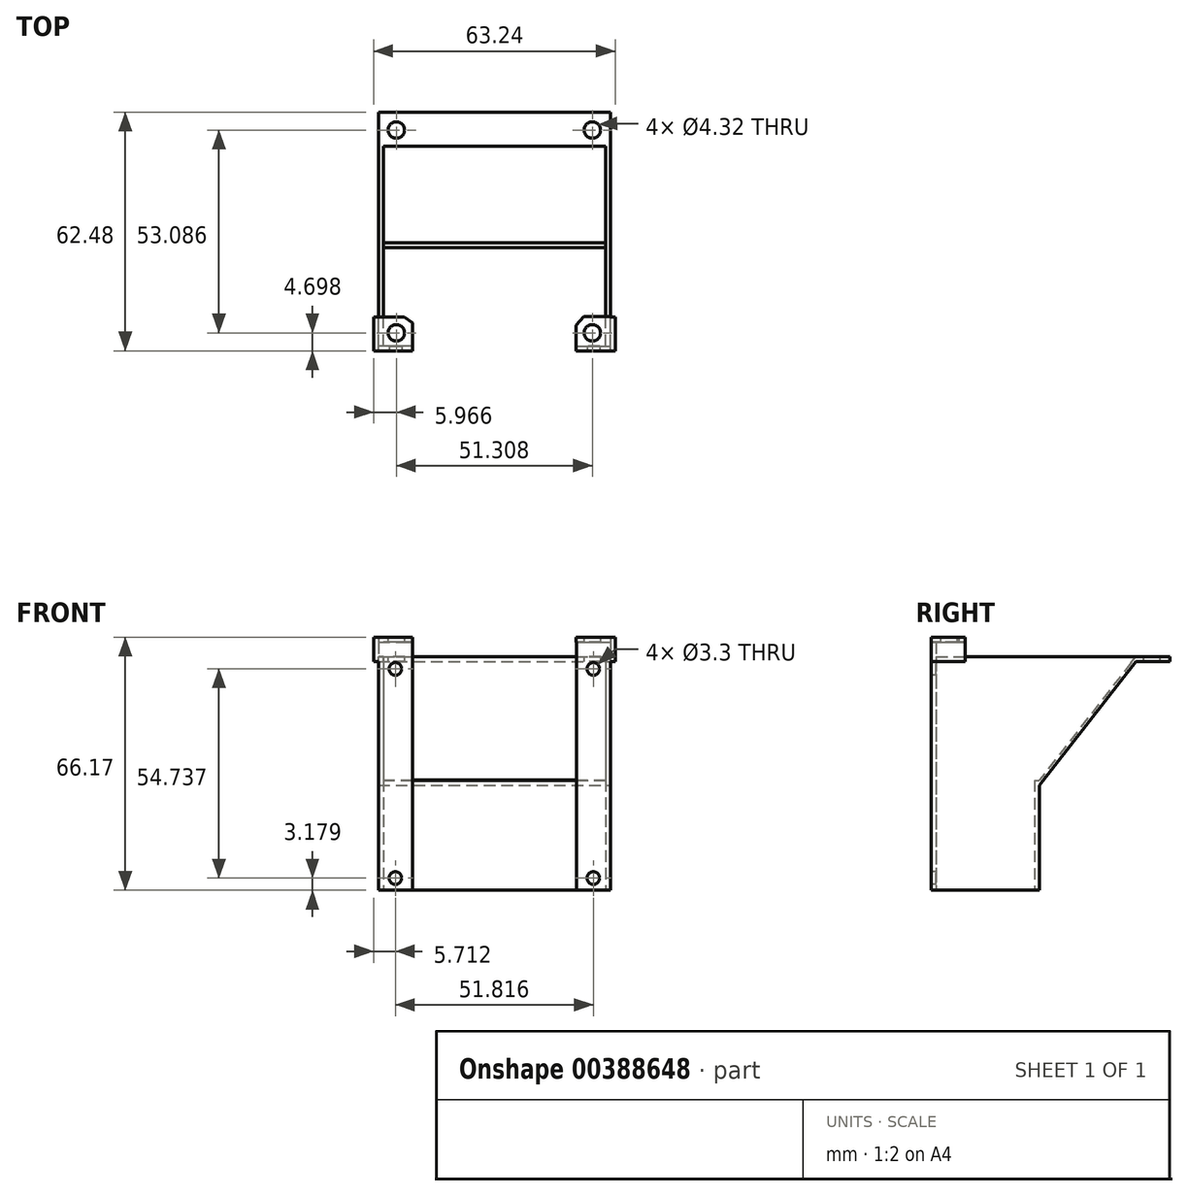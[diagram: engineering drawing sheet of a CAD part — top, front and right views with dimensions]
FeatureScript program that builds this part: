
annotation { "Feature Type Name" : "Feature", "Feature Type Description" : "" }
export const myFeature = defineFeature(function(context is Context, id is Id, definition is map)
    precondition{}
    {
        {
            var Q0;
            Q0=qCreatedBy(makeId("Front.planeOp"),FACE);
            var sketch = newSketch(context, id + "F0", { "sketchPlane" : qUnion([Q0])});
            skLineSegment(sketch, "E0.bottom", {"start": v(-29.08, 14.38) * mm, "end": v(29.08, 14.38) * mm});
            skLineSegment(sketch, "E0.top", {"start": v(-29.08, -14.38) * mm, "end": v(29.08, -14.38) * mm});
            skLineSegment(sketch, "E0.left", {"start": v(-29.08, 14.38) * mm, "end": v(-29.08, -14.38) * mm});
            skLineSegment(sketch, "E0.right", {"start": v(29.08, 14.38) * mm, "end": v(29.08, -14.38) * mm});
            skPoint(sketch, "E0.middle", {"position": v(0, 0) * mm});
            skLineSegment(sketch, "E1.bottom", {"start": v(29.08, -14.38) * mm, "end": v(30.35, -14.38) * mm});
            skLineSegment(sketch, "E1.top", {"start": v(29.08, 46.71) * mm, "end": v(30.35, 46.71) * mm});
            skLineSegment(sketch, "E1.left", {"start": v(29.08, -14.38) * mm, "end": v(29.08, 46.71) * mm});
            skLineSegment(sketch, "E1.right", {"start": v(30.35, -14.38) * mm, "end": v(30.35, 46.71) * mm});
            skLineSegment(sketch, "E2.bottom", {"start": v(-29.08, -14.38) * mm, "end": v(-30.35, -14.38) * mm});
            skLineSegment(sketch, "E2.top", {"start": v(-29.08, 46.71) * mm, "end": v(-30.35, 46.71) * mm});
            skLineSegment(sketch, "E2.left", {"start": v(-29.08, -14.38) * mm, "end": v(-29.08, 46.71) * mm});
            skLineSegment(sketch, "E2.right", {"start": v(-30.35, -14.38) * mm, "end": v(-30.35, 46.71) * mm});
            skSolve(sketch);
        }
        {
            var Q0;
            {var subQ0=sQuery(id+"F0.wireOp",EDGE,"E0.bottom");Q0=makeQuery(id+"F0.imprint","IMPRINT",FACE,{"disambiguationData":[TD([[makeQuery(id+"F0.imprint","IMPRINT",EDGE,{"derivedFrom":subQ0}),-1.0]])]});}
            extrude(context, id + "F1", {"entities" : qUnion([Q0]), "depth" : 1.27 * mm});
        }
        {
            var Q0;
            {var subQ3=sQuery(id+"F0.wireOp",EDGE,"E1.bottom");Q0=makeQuery(id+"F0.imprint","IMPRINT",FACE,{"disambiguationData":[TD([[makeQuery(id+"F0.imprint","IMPRINT",EDGE,{"derivedFrom":subQ3}),1.0]])]});}
            var Q1;
            {var subQ3=sQuery(id+"F0.wireOp",EDGE,"E2.bottom");Q1=makeQuery(id+"F0.imprint","IMPRINT",FACE,{"disambiguationData":[TD([[makeQuery(id+"F0.imprint","IMPRINT",EDGE,{"derivedFrom":subQ3}),-1.0]])]});}
            extrude(context, id + "F2", {"entities" : qUnion([Q0, Q1]), "operationType" : NewBodyOperationType.ADD, "depth" : 28.32 * mm});
        }
        {
            var Q0;
            Q0=makeQuery(id+"F2.opExtrude","SWEPT_FACE",FACE,{"disambiguationData":[OSD([sQuery(id+"F0.wireOp",EDGE,"E1.right")])]});
            var sketch = newSketch(context, id + "F3", { "sketchPlane" : qUnion([Q0])});
            skLineSegment(sketch, "E3.bottom", {"start": v(0, 46.71) * mm, "end": v(34.16, 46.71) * mm});
            skLineSegment(sketch, "E3.right", {"start": v(34.16, 46.71) * mm, "end": v(34.16, 45.44) * mm});
            skLineSegment(sketch, "E4", {"start": v(0, 13.1) * mm, "end": v(25.27, 45.44) * mm});
            skLineSegment(sketch, "E5", {"start": v(24.04, 45.16) * mm, "end": v(0, 14.4) * mm});
            skLineSegment(sketch, "E6", {"start": v(24.04, 45.16) * mm, "end": v(25.27, 46.71) * mm});
            skLineSegment(sketch, "E7", {"start": v(25.27, 45.44) * mm, "end": v(34.16, 45.44) * mm});
            skLineSegment(sketch, "E8", {"start": v(0, 46.71) * mm, "end": v(0, 14.4) * mm});
            skSolve(sketch);
        }
        {
            var Q0;
            {var subQ0=sQuery(id+"F3.wireOp",EDGE,"E4");Q0=makeQuery(id+"F3.imprint","IMPRINT",FACE,{"disambiguationData":[TD([[makeQuery(id+"F3.imprint","IMPRINT",EDGE,{"derivedFrom":subQ0}),1.0]])]});}
            extrude(context, id + "F4", {"entities" : qUnion([Q0]), "operationType" : NewBodyOperationType.ADD, "oppositeDirection" : true, "depth" : 60.7 * mm});
        }
        {
            var Q0;
            Q0=makeQuery(id+"F3.imprint","IMPRINT",FACE,{"disambiguationData":[TD([[makeQuery(id+"F3.imprint","IMPRINT",EDGE,{"derivedFrom":sQuery(id+"F3.wireOp",EDGE,"E5")}),-1.0]])]});
            extrude(context, id + "F5", {"entities" : qUnion([Q0]), "operationType" : NewBodyOperationType.ADD, "oppositeDirection" : true, "depth" : 1.27 * mm});
        }
        {
            var Q0;
            Q0=makeQuery(id+"F4.boolean.opBoolean","MERGE",FACE,{"derivedFrom":[makeQuery(id+"F2.opExtrude","SWEPT_FACE",FACE,{"disambiguationData":[OSD([sQuery(id+"F0.wireOp",EDGE,"E2.right")])]}),makeQuery(id+"F4.opExtrude","CAP_FACE",FACE,{"disambiguationData":[OSD([sQuery(id+"F0.wireOp",EDGE,"E1.right"),sQuery(id+"F3.wireOp",EDGE,"E3.bottom"),sQuery(id+"F3.wireOp",EDGE,"E3.right"),sQuery(id+"F3.wireOp",EDGE,"E4"),sQuery(id+"F3.wireOp",EDGE,"E5"),sQuery(id+"F3.wireOp",EDGE,"E6"),sQuery(id+"F3.wireOp",EDGE,"E7")])],"isStart":false})]});
            var sketch = newSketch(context, id + "F6", { "sketchPlane" : qUnion([Q0])});
            skLineSegment(sketch, "E9", {"start": v(-25.27, 46.71) * mm, "end": v(0, 46.71) * mm});
            skLineSegment(sketch, "E10", {"start": v(0, 46.71) * mm, "end": v(0, 14.4) * mm});
            skLineSegment(sketch, "E11", {"start": v(0, 14.4) * mm, "end": v(-25.27, 46.71) * mm});
            skSolve(sketch);
        }
        {
            var Q0;
            Q0=qSketchRegion(id+"F6",true);
            extrude(context, id + "F7", {"entities" : qUnion([Q0]), "operationType" : NewBodyOperationType.ADD, "oppositeDirection" : true, "depth" : 1.27 * mm});
        }
        {
            var Q0;
            {var subQ0=sQuery(id+"F3.wireOp",EDGE,"E3.bottom");Q0=makeQuery(id+"F7.boolean.opBoolean","MERGE",FACE,{"derivedFrom":[makeQuery(id+"F2.opExtrude","SWEPT_FACE",FACE,{"disambiguationData":[OSD([sQuery(id+"F0.wireOp",EDGE,"E2.top")])]}),makeQuery(id+"F5.boolean.opBoolean","MERGE",FACE,{"derivedFrom":[makeQuery(id+"F2.opExtrude","SWEPT_FACE",FACE,{"disambiguationData":[OSD([sQuery(id+"F0.wireOp",EDGE,"E1.top")])]}),makeQuery(id+"F4.opExtrude","SWEPT_FACE",FACE,{"disambiguationData":[OSD([subQ0])]}),makeQuery(id+"F5.opExtrude","SWEPT_FACE",FACE,{"disambiguationData":[OSD([subQ0])]})]}),makeQuery(id+"F7.opExtrude","SWEPT_FACE",FACE,{"disambiguationData":[OSD([sQuery(id+"F6.wireOp",EDGE,"E9")])]})]});}
            var sketch = newSketch(context, id + "F8", { "sketchPlane" : qUnion([Q0])});
            skCircle(sketch, "E12", {"center": v(-25.65, 29.46) * mm, "radius": 2.16 * mm});
            skCircle(sketch, "E13", {"center": v(25.65, 29.46) * mm, "radius": 2.16 * mm});
            skSolve(sketch);
        }
        {
            var Q0;
            Q0=qSketchRegion(id+"F8",true);
            extrude(context, id + "F9", {"entities" : qUnion([Q0]), "operationType" : NewBodyOperationType.REMOVE, "oppositeDirection" : true, "depth" : 1.27 * mm});
        }
        {
            var Q0;
            Q0=makeQuery(id+"F5.boolean.opBoolean","MERGE",FACE,{"derivedFrom":[makeQuery(id+"F2.opExtrude","SWEPT_FACE",FACE,{"disambiguationData":[OSD([sQuery(id+"F0.wireOp",EDGE,"E1.left")])]}),makeQuery(id+"F5.opExtrude","CAP_FACE",FACE,{"disambiguationData":[OSD([sQuery(id+"F3.wireOp",EDGE,"E3.bottom"),sQuery(id+"F3.wireOp",EDGE,"E5"),sQuery(id+"F3.wireOp",EDGE,"E6"),sQuery(id+"F3.wireOp",EDGE,"E8")])],"isStart":false})]});
            var sketch = newSketch(context, id + "F10", { "sketchPlane" : qUnion([Q0])});
            skLineSegment(sketch, "E14.bottom", {"start": v(28.32, 46.71) * mm, "end": v(27.05, 46.71) * mm});
            skLineSegment(sketch, "E14.top", {"start": v(28.32, -14.38) * mm, "end": v(27.05, -14.38) * mm});
            skLineSegment(sketch, "E14.left", {"start": v(28.32, 46.71) * mm, "end": v(28.32, -14.38) * mm});
            skLineSegment(sketch, "E14.right", {"start": v(27.05, 46.71) * mm, "end": v(27.05, -14.38) * mm});
            skSolve(sketch);
        }
        {
            var Q0;
            Q0=qSketchRegion(id+"F10",true);
            extrude(context, id + "F11", {"entities" : qUnion([Q0]), "operationType" : NewBodyOperationType.ADD, "depth" : 7.62 * mm});
        }
        {
            var Q0;
            Q0=makeQuery(id+"F7.boolean.opBoolean","MERGE",FACE,{"derivedFrom":[makeQuery(id+"F2.opExtrude","SWEPT_FACE",FACE,{"disambiguationData":[OSD([sQuery(id+"F0.wireOp",EDGE,"E2.left")])]}),makeQuery(id+"F7.opExtrude","CAP_FACE",FACE,{"disambiguationData":[OSD([sQuery(id+"F6.wireOp",EDGE,"E9"),sQuery(id+"F6.wireOp",EDGE,"E10"),sQuery(id+"F6.wireOp",EDGE,"E11")])],"isStart":false})]});
            var sketch = newSketch(context, id + "F12", { "sketchPlane" : qUnion([Q0])});
            skLineSegment(sketch, "E15.bottom", {"start": v(-28.32, 46.71) * mm, "end": v(-27.05, 46.71) * mm});
            skLineSegment(sketch, "E15.top", {"start": v(-28.32, -14.38) * mm, "end": v(-27.05, -14.38) * mm});
            skLineSegment(sketch, "E15.left", {"start": v(-28.32, 46.71) * mm, "end": v(-28.32, -14.38) * mm});
            skLineSegment(sketch, "E15.right", {"start": v(-27.05, 46.71) * mm, "end": v(-27.05, -14.38) * mm});
            skSolve(sketch);
        }
        {
            var Q0;
            Q0=qSketchRegion(id+"F12",true);
            extrude(context, id + "F13", {"entities" : qUnion([Q0]), "operationType" : NewBodyOperationType.ADD, "depth" : 7.62 * mm});
        }
        {
            var Q0;
            Q0=makeQuery(id+"F13.boolean.opBoolean","MERGE",FACE,{"derivedFrom":[makeQuery(id+"F2.opExtrude","CAP_FACE",FACE,{"disambiguationData":[OSD([sQuery(id+"F0.wireOp",EDGE,"E2.bottom"),sQuery(id+"F0.wireOp",EDGE,"E2.top"),sQuery(id+"F0.wireOp",EDGE,"E2.left"),sQuery(id+"F0.wireOp",EDGE,"E2.right")])],"isStart":false}),makeQuery(id+"F13.opExtrude","SWEPT_FACE",FACE,{"disambiguationData":[OSD([sQuery(id+"F12.wireOp",EDGE,"E15.left")])]})]});
            var sketch = newSketch(context, id + "F14", { "sketchPlane" : qUnion([Q0])});
            skCircle(sketch, "E16", {"center": v(-25.9, 43.54) * mm, "radius": 1.65 * mm});
            skCircle(sketch, "E17", {"center": v(25.9, 43.54) * mm, "radius": 1.65 * mm});
            skCircle(sketch, "E18", {"center": v(-25.9, -11.2) * mm, "radius": 1.65 * mm});
            skCircle(sketch, "E19", {"center": v(25.9, -11.2) * mm, "radius": 1.65 * mm});
            skSolve(sketch);
        }
        {
            var Q0;
            Q0=makeQuery(id+"F14.imprint","IMPRINT",FACE,{"disambiguationData":[TD([[makeQuery(id+"F14.imprint","IMPRINT",EDGE,{"derivedFrom":sQuery(id+"F14.wireOp",EDGE,"E19")}),1.0]])]});
            var Q1;
            Q1=makeQuery(id+"F14.imprint","IMPRINT",FACE,{"disambiguationData":[TD([[makeQuery(id+"F14.imprint","IMPRINT",EDGE,{"derivedFrom":sQuery(id+"F14.wireOp",EDGE,"E18")}),1.0]])]});
            var Q2;
            Q2=makeQuery(id+"F14.imprint","IMPRINT",FACE,{"disambiguationData":[TD([[makeQuery(id+"F14.imprint","IMPRINT",EDGE,{"derivedFrom":sQuery(id+"F14.wireOp",EDGE,"E16")}),1.0]])]});
            var Q3;
            Q3=makeQuery(id+"F14.imprint","IMPRINT",FACE,{"disambiguationData":[TD([[makeQuery(id+"F14.imprint","IMPRINT",EDGE,{"derivedFrom":sQuery(id+"F14.wireOp",EDGE,"E17")}),1.0]])]});
            extrude(context, id + "F15", {"entities" : qUnion([Q0, Q1, Q2, Q3]), "operationType" : NewBodyOperationType.REMOVE, "oppositeDirection" : true, "depth" : 1.27 * mm});
        }
        {
            var Q0;
            {var subQ0=sQuery(id+"F3.wireOp",EDGE,"E3.bottom");Q0=makeQuery(id+"F13.boolean.opBoolean","MERGE",FACE,{"derivedFrom":[makeQuery(id+"F11.boolean.opBoolean","MERGE",FACE,{"derivedFrom":[makeQuery(id+"F7.boolean.opBoolean","MERGE",FACE,{"derivedFrom":[makeQuery(id+"F2.opExtrude","SWEPT_FACE",FACE,{"disambiguationData":[OSD([sQuery(id+"F0.wireOp",EDGE,"E2.top")])]}),makeQuery(id+"F5.boolean.opBoolean","MERGE",FACE,{"derivedFrom":[makeQuery(id+"F2.opExtrude","SWEPT_FACE",FACE,{"disambiguationData":[OSD([sQuery(id+"F0.wireOp",EDGE,"E1.top")])]}),makeQuery(id+"F4.opExtrude","SWEPT_FACE",FACE,{"disambiguationData":[OSD([subQ0])]}),makeQuery(id+"F5.opExtrude","SWEPT_FACE",FACE,{"disambiguationData":[OSD([subQ0])]})]}),makeQuery(id+"F7.opExtrude","SWEPT_FACE",FACE,{"disambiguationData":[OSD([sQuery(id+"F6.wireOp",EDGE,"E9")])]})]}),makeQuery(id+"F11.opExtrude","SWEPT_FACE",FACE,{"disambiguationData":[OSD([sQuery(id+"F10.wireOp",EDGE,"E14.bottom")])]})]}),makeQuery(id+"F13.opExtrude","SWEPT_FACE",FACE,{"disambiguationData":[OSD([sQuery(id+"F12.wireOp",EDGE,"E15.bottom")])]})]});}
            var sketch = newSketch(context, id + "F16", { "sketchPlane" : qUnion([Q0])});
            skLineSegment(sketch, "E20.bottom", {"start": v(-21.46, -28.32) * mm, "end": v(-30.35, -28.32) * mm});
            skLineSegment(sketch, "E20.top", {"start": v(-21.46, -27.05) * mm, "end": v(-30.35, -27.05) * mm});
            skLineSegment(sketch, "E20.left", {"start": v(-21.46, -28.32) * mm, "end": v(-21.46, -27.05) * mm});
            skLineSegment(sketch, "E20.right", {"start": v(-30.35, -28.32) * mm, "end": v(-30.35, -27.05) * mm});
            skLineSegment(sketch, "E21.bottom", {"start": v(21.46, -28.32) * mm, "end": v(30.35, -28.32) * mm});
            skLineSegment(sketch, "E21.top", {"start": v(21.46, -27.05) * mm, "end": v(30.35, -27.05) * mm});
            skLineSegment(sketch, "E21.left", {"start": v(21.46, -28.32) * mm, "end": v(21.46, -27.05) * mm});
            skLineSegment(sketch, "E21.right", {"start": v(30.35, -28.32) * mm, "end": v(30.35, -27.05) * mm});
            skSolve(sketch);
        }
        {
            var Q0;
            Q0=makeQuery(id+"F16.imprint","IMPRINT",FACE,{"disambiguationData":[TD([[makeQuery(id+"F16.imprint","IMPRINT",EDGE,{"derivedFrom":sQuery(id+"F16.wireOp",EDGE,"iGthfG7R-L8Vh-ynzw-XpxA-xoLUt4kfoV39.bottom")}),1.0]])]});
            var Q1;
            Q1=makeQuery(id+"F16.imprint","IMPRINT",FACE,{"disambiguationData":[TD([[makeQuery(id+"F16.imprint","IMPRINT",EDGE,{"derivedFrom":sQuery(id+"F16.wireOp",EDGE,"E20.bottom")}),-1.0]])]});
            var Q2;
            Q2=makeQuery(id+"F16.imprint","IMPRINT",FACE,{"disambiguationData":[TD([[makeQuery(id+"F16.imprint","IMPRINT",EDGE,{"derivedFrom":sQuery(id+"F16.wireOp",EDGE,"E21.bottom")}),1.0]])]});
            var Q3;
            Q3=makeQuery(id+"F16.imprint","IMPRINT",FACE,{"disambiguationData":[TD([[makeQuery(id+"F16.imprint","IMPRINT",EDGE,{"derivedFrom":sQuery(id+"F16.wireOp",EDGE,"lIkf934W-Q6BH-iXOC-zUm2-EJspjA8qrpHl.bottom")}),-1.0]])]});
            extrude(context, id + "F17", {"entities" : qUnion([Q0, Q1, Q2, Q3]), "operationType" : NewBodyOperationType.ADD, "depth" : 3.8 * mm});
        }
        {
            var Q0;
            Q0=makeQuery(id+"F17.opExtrude","CAP_FACE",FACE,{"disambiguationData":[OSD([sQuery(id+"F16.wireOp",EDGE,"E20.bottom"),sQuery(id+"F16.wireOp",EDGE,"E20.top"),sQuery(id+"F16.wireOp",EDGE,"E20.left"),sQuery(id+"F16.wireOp",EDGE,"E20.right"),sQuery(id+"F16.wireOp",EDGE,"iGthfG7R-L8Vh-ynzw-XpxA-xoLUt4kfoV39.top"),sQuery(id+"F16.wireOp",EDGE,"iGthfG7R-L8Vh-ynzw-XpxA-xoLUt4kfoV39.left"),sQuery(id+"F16.wireOp",EDGE,"iGthfG7R-L8Vh-ynzw-XpxA-xoLUt4kfoV39.right")])],"isStart":false});
            var sketch = newSketch(context, id + "F18", { "sketchPlane" : qUnion([Q0])});
            skLineSegment(sketch, "E22.bottom", {"start": v(-30.35, -28.32) * mm, "end": v(-21.46, -28.32) * mm});
            skLineSegment(sketch, "E22.left", {"start": v(-30.35, -28.32) * mm, "end": v(-30.35, -19.42) * mm});
            skLineSegment(sketch, "E23", {"start": v(-23.61, -19.42) * mm, "end": v(-21.46, -21.04) * mm});
            skLineSegment(sketch, "E24", {"start": v(-30.35, -19.42) * mm, "end": v(-23.61, -19.42) * mm});
            skLineSegment(sketch, "E25", {"start": v(-21.46, -21.04) * mm, "end": v(-21.46, -28.32) * mm});
            skLineSegment(sketch, "E26.bottom", {"start": v(-30.35, -28.32) * mm, "end": v(-31.62, -28.32) * mm});
            skLineSegment(sketch, "E26.top", {"start": v(-30.35, -19.43) * mm, "end": v(-31.62, -19.43) * mm});
            skLineSegment(sketch, "E26.left", {"start": v(-30.35, -28.32) * mm, "end": v(-30.35, -19.43) * mm});
            skLineSegment(sketch, "E26.right", {"start": v(-31.62, -28.32) * mm, "end": v(-31.62, -19.43) * mm});
            skSolve(sketch);
        }
        {
            var Q0;
            Q0=qSketchRegion(id+"F18",true);
            extrude(context, id + "F19", {"entities" : qUnion([Q0]), "operationType" : NewBodyOperationType.ADD, "depth" : 1.27 * mm});
        }
        {
            var Q0;
            Q0=makeQuery(id+"F17.opExtrude","CAP_FACE",FACE,{"disambiguationData":[OSD([sQuery(id+"F16.wireOp",EDGE,"E21.bottom"),sQuery(id+"F16.wireOp",EDGE,"E21.top"),sQuery(id+"F16.wireOp",EDGE,"E21.left"),sQuery(id+"F16.wireOp",EDGE,"E21.right"),sQuery(id+"F16.wireOp",EDGE,"lIkf934W-Q6BH-iXOC-zUm2-EJspjA8qrpHl.top"),sQuery(id+"F16.wireOp",EDGE,"lIkf934W-Q6BH-iXOC-zUm2-EJspjA8qrpHl.left"),sQuery(id+"F16.wireOp",EDGE,"lIkf934W-Q6BH-iXOC-zUm2-EJspjA8qrpHl.right")])],"isStart":false});
            var sketch = newSketch(context, id + "F20", { "sketchPlane" : qUnion([Q0])});
            skLineSegment(sketch, "E27.bottom", {"start": v(30.35, -28.32) * mm, "end": v(21.42, -28.32) * mm});
            skLineSegment(sketch, "E27.left", {"start": v(30.35, -28.32) * mm, "end": v(30.35, -19.38) * mm});
            skLineSegment(sketch, "E28", {"start": v(23.4, -19.38) * mm, "end": v(21.42, -21.59) * mm});
            skLineSegment(sketch, "E29", {"start": v(21.42, -21.59) * mm, "end": v(21.42, -28.32) * mm});
            skLineSegment(sketch, "E30", {"start": v(23.4, -19.38) * mm, "end": v(30.35, -19.38) * mm});
            skLineSegment(sketch, "E31.bottom", {"start": v(30.35, -28.32) * mm, "end": v(31.62, -28.32) * mm});
            skLineSegment(sketch, "E31.top", {"start": v(30.35, -19.43) * mm, "end": v(31.62, -19.43) * mm});
            skLineSegment(sketch, "E31.left", {"start": v(30.35, -28.32) * mm, "end": v(30.35, -19.43) * mm});
            skLineSegment(sketch, "E31.right", {"start": v(31.62, -28.32) * mm, "end": v(31.62, -19.43) * mm});
            skSolve(sketch);
        }
        {
            var Q0;
            Q0=qSketchRegion(id+"F20",true);
            extrude(context, id + "F21", {"entities" : qUnion([Q0]), "operationType" : NewBodyOperationType.ADD, "depth" : 1.27 * mm});
        }
        {
            var Q0;
            Q0=makeQuery(id+"F19.opExtrude","CAP_FACE",FACE,{"disambiguationData":[OSD([sQuery(id+"F18.wireOp",EDGE,"E22.bottom"),sQuery(id+"F18.wireOp",EDGE,"E22.top"),sQuery(id+"F18.wireOp",EDGE,"E22.left"),sQuery(id+"F18.wireOp",EDGE,"E22.right")])],"isStart":false});
            var sketch = newSketch(context, id + "F22", { "sketchPlane" : qUnion([Q0])});
            skPoint(sketch, "E32.centerSnap0", {"position": v(-26.54, -28.32) * mm});
            skCircle(sketch, "E33", {"center": v(-25.65, -23.62) * mm, "radius": 2.16 * mm});
            skCircle(sketch, "E34", {"center": v(25.65, -23.62) * mm, "radius": 2.16 * mm});
            skSolve(sketch);
        }
        {
            var Q0;
            Q0=qSketchRegion(id+"F22",true);
            extrude(context, id + "F23", {"entities" : qUnion([Q0]), "operationType" : NewBodyOperationType.REMOVE, "oppositeDirection" : true, "depth" : 1.27 * mm});
        }
        {
            var Q0;
            Q0=qSketchRegion(id+"F22",true);
            extrude(context, id + "F24", {"entities" : qUnion([Q0]), "operationType" : NewBodyOperationType.REMOVE, "oppositeDirection" : true, "depth" : 1.27 * mm});
        }
        {
            var Q0;
            Q0=qSketchRegion(id+"F8",true);
            extrude(context, id + "F25", {"entities" : qUnion([Q0]), "operationType" : NewBodyOperationType.REMOVE, "oppositeDirection" : true, "depth" : 12.7 * mm});
        }
        {
            var Q0;
            {var subQ1=sQuery(id+"F18.wireOp",EDGE,"E26.bottom");Q0=makeQuery(id+"F18.imprint","IMPRINT",FACE,{"disambiguationData":[TD([[makeQuery(id+"F18.imprint","IMPRINT",EDGE,{"derivedFrom":subQ1}),-1.0]])]});}
            extrude(context, id + "F26", {"entities" : qUnion([Q0]), "operationType" : NewBodyOperationType.ADD, "oppositeDirection" : true, "depth" : 5.08 * mm});
        }
        {
            var Q0;
            {var subQ1=sQuery(id+"F20.wireOp",EDGE,"E31.bottom");Q0=makeQuery(id+"F20.imprint","IMPRINT",FACE,{"disambiguationData":[TD([[makeQuery(id+"F20.imprint","IMPRINT",EDGE,{"derivedFrom":subQ1}),1.0]])]});}
            extrude(context, id + "F27", {"entities" : qUnion([Q0]), "operationType" : NewBodyOperationType.ADD, "oppositeDirection" : true, "depth" : 5.08 * mm});
        }
    });
